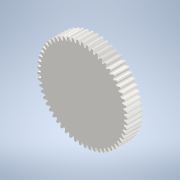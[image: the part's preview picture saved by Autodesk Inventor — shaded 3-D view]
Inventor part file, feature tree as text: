
AUTODESK INVENTOR PART (.ipt)
format: ipt  version: 2022 (Build 260153000, 153)  size: 375,296 bytes
history: native  units: mm (DEFAULTED — no unit token found)
features: plane x3, other x3, sketch x2, extrude x1
ambient origin geometry x8: Origin, YZ Plane, XZ Plane, XY Plane, X Axis, Y Axis, Z Axis, Center Point
bodies: Solid1 (feature_tree)
feature tree (9):
  extrude  "Extrusion1"  Depth=25.4mm TaperAngle=0.0deg
  plane  "Work Plane1"
  plane  "Work Plane2"
  plane  "Work Plane3"
  other  "Spur Gear"
  sketch  "Sketch1"  dims[d0=149.86mm d1=25.4mm d2=0.0mm]
  sketch  "Sketch2"  dims[d3=144.78mm d4=76.2mm d5=0.0mm d6=0.0mm d7=0.551157mm d9=0.0mm d14=0.0mm d15=101.6mm d16=0.0mm d17=0.0mm d18=0.0mm d19=101.6mm]
  other  "Srf1"
  other  "Pitch Diameter"
